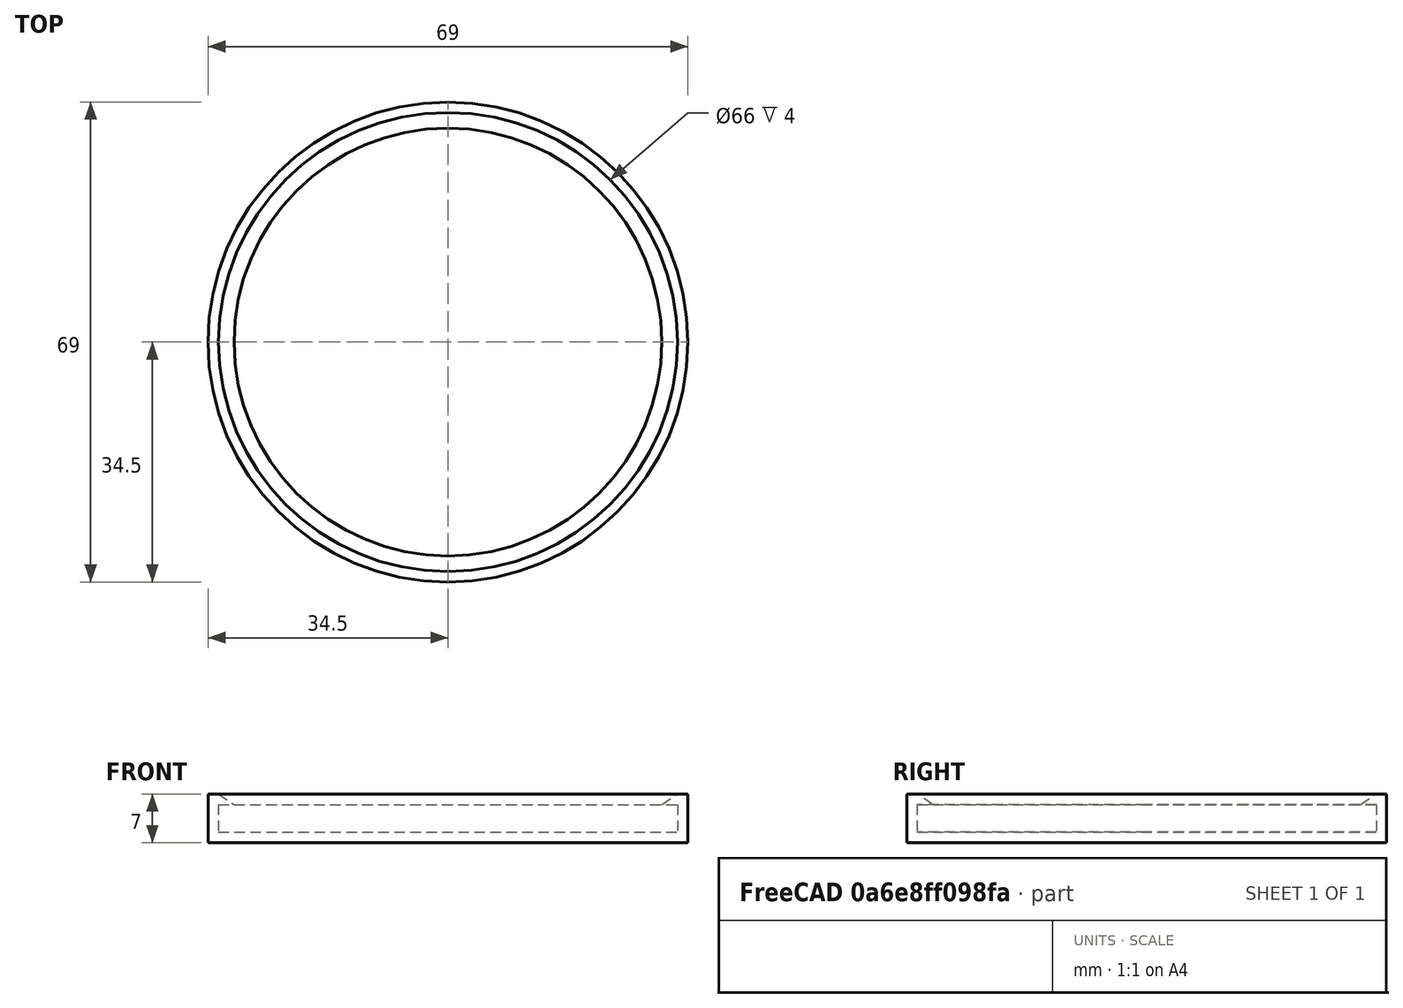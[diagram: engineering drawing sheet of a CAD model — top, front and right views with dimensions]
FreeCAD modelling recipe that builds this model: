
FCSTD DOCUMENT  (FreeCAD 0.20R29177 +426 (Git))
Label: pet_food_lid_65mm
License: Creative Commons Attribution
LicenseURL: http://creativecommons.org/licenses/by/3.0/
objects: Sketcher::SketchObject×1, PartDesign::Revolution×1, PartDesign::Body×1, Mesh::Feature×1
note: 4 computed .brp shape members not serialized (recipe doc carries the construction recipe); baked Part::Feature solids carry a one-line shape summary decoded from their .brp

FEATURE [Sketcher::SketchObject] Sketch
  FullyConstrained = true
  MapMode = 5
  Placement = pos=(0,0,0) rot=(1,0,0;1.5708rad)
  Support = -> [XZ_Plane]
  expr: .Constraints.CanRadius = 61.51 / 2
  expr: .Constraints.LidRadius = 66 / 2
  expr: Constraints[21] = .Constraints.top_thickness * 2 + .Constraints.rim_thickness
  expr: Constraints[22] = .Constraints.top_thickness
  sketch-geometry (8):
    g0: LineSegment StartX=0 StartY=0 StartZ=0 EndX=-34.5 EndY=0 EndZ=0
    g1: LineSegment StartX=-34.5 StartY=0 StartZ=0 EndX=-34.5 EndY=7 EndZ=0
    g2: LineSegment StartX=-34.5 StartY=7 StartZ=0 EndX=-33 EndY=7 EndZ=0
    g3: LineSegment StartX=-33 StartY=7 StartZ=0 EndX=-30.755 EndY=5.5 EndZ=0
    g4: LineSegment StartX=-30.755 StartY=5.5 StartZ=0 EndX=-33 EndY=5.5 EndZ=0
    g5: LineSegment StartX=-33 StartY=5.5 StartZ=0 EndX=-33 EndY=1.5 EndZ=0
    g6: LineSegment StartX=-33 StartY=1.5 StartZ=0 EndX=0 EndY=1.5 EndZ=0
    g7: LineSegment StartX=0 StartY=1.5 StartZ=0 EndX=0 EndY=0 EndZ=0
  constraints (23):
    c: Coincident(g-1,g0)
    c: PointOnObject(g0,g-1)
    c: Coincident(g0,g1)
    c: Vertical(g1)
    c: Coincident(g1,g2)
    c: Horizontal(g2)
    c: Coincident(g2,g3)
    c: Coincident(g3,g4)
    c: Horizontal(g4)
    c: Coincident(g4,g5)
    c: Vertical(g5)
    c: Coincident(g5,g6)
    c: PointOnObject(g6,g-2)
    c: Horizontal(g6)
    c: Coincident(g6,g7)
    c: Coincident(g7,g0)
    c: DistanceX(g5,g6) = 33  'LidRadius'
    c: DistanceY(g0,g6) = 1.5  'top_thickness'
    c: DistanceX(g0,g5) = 1.5
    c: DistanceX(g3,g6) = 30.755  'CanRadius'
    c: DistanceY(g5,g4) = 4  'rim_thickness'
    c: DistanceY(g0,g1) = 7
    c: DistanceX(g1,g2) = 1.5
FEATURE [PartDesign::Revolution] Revolution
  Angle = 360
  Axis = (0,-2e-16,1)
  Base = (0,0,0)
  Placement = pos=(0,0,0) rot=(1,0,0;1.5708rad)
  Profile = -> Sketch
  ReferenceAxis = -> Sketch [V_Axis]
FEATURE [PartDesign::Body] Body
  Group = -> [Sketch,Revolution]
  Origin = -> Origin
  Tip = -> Revolution
FEATURE [Mesh::Feature] Mesh  label="pet_food_lid_65mm"
